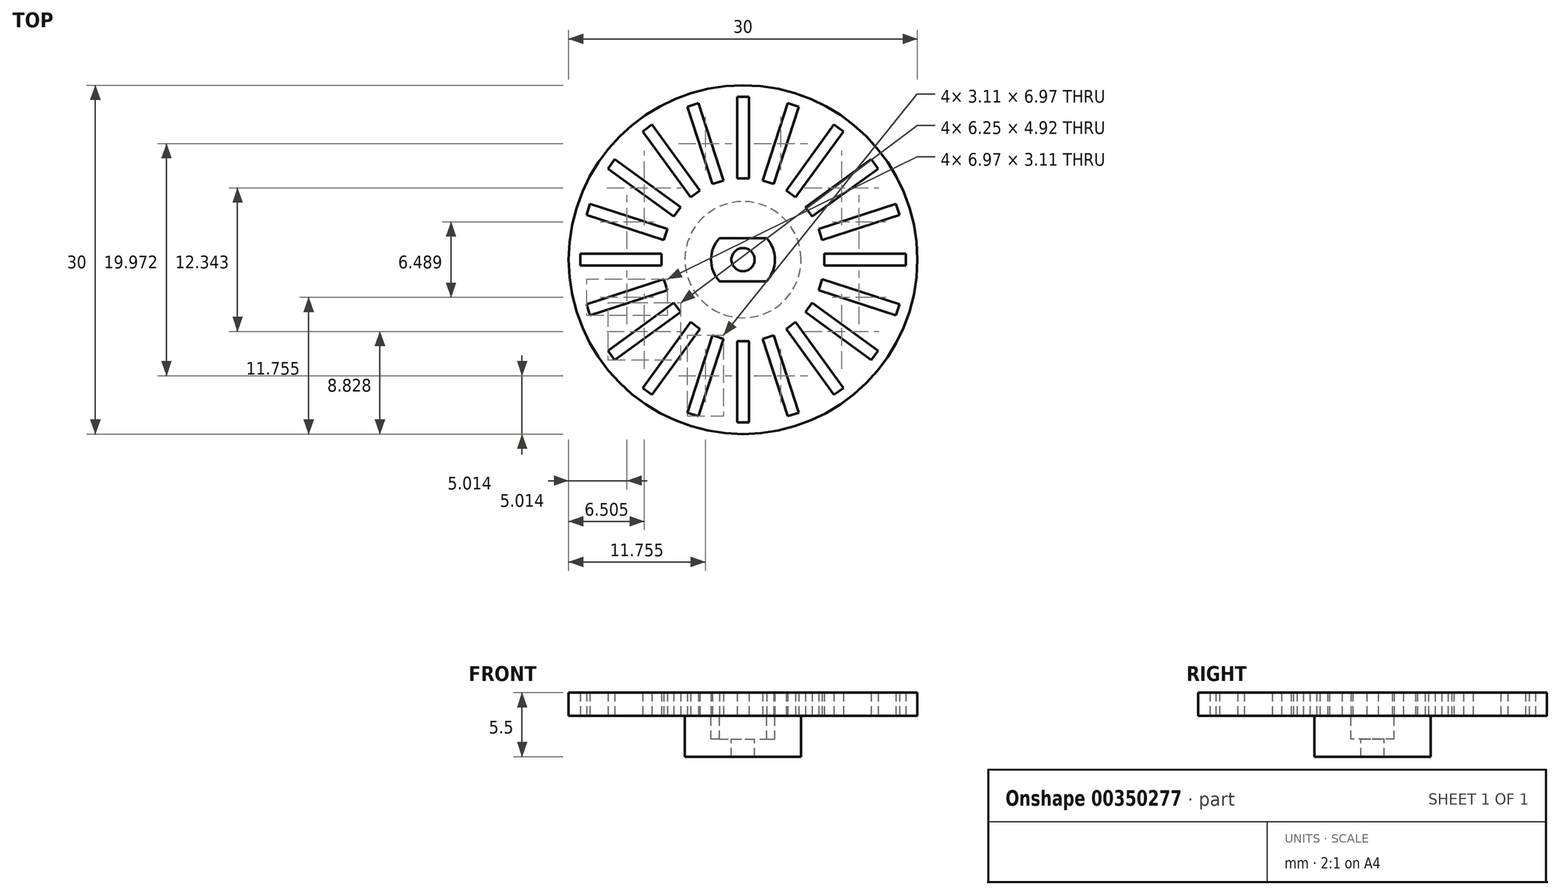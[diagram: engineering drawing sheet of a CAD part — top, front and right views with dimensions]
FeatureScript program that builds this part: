
annotation { "Feature Type Name" : "Feature", "Feature Type Description" : "" }
export const myFeature = defineFeature(function(context is Context, id is Id, definition is map)
    precondition{}
    {
        {
            var Q0;
            Q0=qCreatedBy(makeId("Top.planeOp"),FACE);
            var sketch = newSketch(context, id + "F0", { "sketchPlane" : qUnion([Q0])});
            skCircle(sketch, "E0", {"center": v(0, 0) * mm, "radius": 15 * mm});
            skArc(sketch, "E1", {"start": v(-2.03, 1.86) * mm, "mid": v(-2.75, 0) * mm, "end": v(-2.03, -1.86) * mm});
            skLineSegment(sketch, "E2.MirrorCS", {"start": v(-2.03, -1.86) * mm, "end": v(2.03, -1.86) * mm});
            skArc(sketch, "E3.trimOffspring", {"start": v(2.03, -1.86) * mm, "mid": v(2.75, 0) * mm, "end": v(2.03, 1.86) * mm});
            skLineSegment(sketch, "E4.MirrorCS", {"start": v(-2.03, 1.86) * mm, "end": v(2.03, 1.86) * mm});
            skLineSegment(sketch, "E5", {"start": v(0, -7) * mm, "end": v(-0.5, -7) * mm});
            skLineSegment(sketch, "E6", {"start": v(-0.5, -7) * mm, "end": v(-0.5, -14) * mm});
            skLineSegment(sketch, "E7", {"start": v(-0.5, -14) * mm, "end": v(0, -14) * mm});
            skLineSegment(sketch, "E8.MirrorCS", {"start": v(0.5, -7) * mm, "end": v(0.5, -14) * mm});
            skLineSegment(sketch, "E9", {"start": v(0, -7) * mm, "end": v(0.5, -7) * mm});
            skLineSegment(sketch, "E10", {"start": v(0, -14) * mm, "end": v(0.5, -14) * mm});
            skLineSegment(sketch, "E11.1.0", {"start": v(1.69, -6.81) * mm, "end": v(3.85, -13.47) * mm});
            skLineSegment(sketch, "E11.1.1", {"start": v(2.64, -6.5) * mm, "end": v(4.8, -13.16) * mm});
            skLineSegment(sketch, "E11.1.2", {"start": v(3.85, -13.47) * mm, "end": v(4.33, -13.31) * mm});
            skLineSegment(sketch, "E11.1.3", {"start": v(2.16, -6.66) * mm, "end": v(2.64, -6.5) * mm});
            skLineSegment(sketch, "E11.1.4", {"start": v(4.33, -13.31) * mm, "end": v(4.8, -13.16) * mm});
            skLineSegment(sketch, "E11.1.5", {"start": v(2.16, -6.66) * mm, "end": v(1.69, -6.81) * mm});
            skLineSegment(sketch, "E11.2.0", {"start": v(3.7, -5.96) * mm, "end": v(7.82, -11.62) * mm});
            skLineSegment(sketch, "E11.2.1", {"start": v(4.52, -5.37) * mm, "end": v(8.63, -11.03) * mm});
            skLineSegment(sketch, "E11.2.2", {"start": v(7.82, -11.62) * mm, "end": v(8.23, -11.33) * mm});
            skLineSegment(sketch, "E11.2.3", {"start": v(4.11, -5.66) * mm, "end": v(4.52, -5.37) * mm});
            skLineSegment(sketch, "E11.2.4", {"start": v(8.23, -11.33) * mm, "end": v(8.63, -11.03) * mm});
            skLineSegment(sketch, "E11.2.5", {"start": v(4.11, -5.66) * mm, "end": v(3.7, -5.96) * mm});
            skLineSegment(sketch, "E11.3.0", {"start": v(5.37, -4.52) * mm, "end": v(11.03, -8.63) * mm});
            skLineSegment(sketch, "E11.3.1", {"start": v(5.96, -3.7) * mm, "end": v(11.62, -7.82) * mm});
            skLineSegment(sketch, "E11.3.2", {"start": v(11.03, -8.63) * mm, "end": v(11.33, -8.23) * mm});
            skLineSegment(sketch, "E11.3.3", {"start": v(5.66, -4.11) * mm, "end": v(5.96, -3.7) * mm});
            skLineSegment(sketch, "E11.3.4", {"start": v(11.33, -8.23) * mm, "end": v(11.62, -7.82) * mm});
            skLineSegment(sketch, "E11.3.5", {"start": v(5.66, -4.11) * mm, "end": v(5.37, -4.52) * mm});
            skLineSegment(sketch, "E11.4.0", {"start": v(6.5, -2.64) * mm, "end": v(13.16, -4.8) * mm});
            skLineSegment(sketch, "E11.4.1", {"start": v(6.81, -1.69) * mm, "end": v(13.47, -3.85) * mm});
            skLineSegment(sketch, "E11.4.2", {"start": v(13.16, -4.8) * mm, "end": v(13.31, -4.33) * mm});
            skLineSegment(sketch, "E11.4.3", {"start": v(6.66, -2.16) * mm, "end": v(6.81, -1.69) * mm});
            skLineSegment(sketch, "E11.4.4", {"start": v(13.31, -4.33) * mm, "end": v(13.47, -3.85) * mm});
            skLineSegment(sketch, "E11.4.5", {"start": v(6.66, -2.16) * mm, "end": v(6.5, -2.64) * mm});
            skLineSegment(sketch, "E11.5.0", {"start": v(7, -0.5) * mm, "end": v(14, -0.5) * mm});
            skLineSegment(sketch, "E11.5.1", {"start": v(7, 0.5) * mm, "end": v(14, 0.5) * mm});
            skLineSegment(sketch, "E11.5.2", {"start": v(14, -0.5) * mm, "end": v(14, 0) * mm});
            skLineSegment(sketch, "E11.5.3", {"start": v(7, 0) * mm, "end": v(7, 0.5) * mm});
            skLineSegment(sketch, "E11.5.4", {"start": v(14, 0) * mm, "end": v(14, 0.5) * mm});
            skLineSegment(sketch, "E11.5.5", {"start": v(7, 0) * mm, "end": v(7, -0.5) * mm});
            skLineSegment(sketch, "E11.6.0", {"start": v(6.81, 1.69) * mm, "end": v(13.47, 3.85) * mm});
            skLineSegment(sketch, "E11.6.1", {"start": v(6.5, 2.64) * mm, "end": v(13.16, 4.8) * mm});
            skLineSegment(sketch, "E11.6.2", {"start": v(13.47, 3.85) * mm, "end": v(13.31, 4.33) * mm});
            skLineSegment(sketch, "E11.6.3", {"start": v(6.66, 2.16) * mm, "end": v(6.5, 2.64) * mm});
            skLineSegment(sketch, "E11.6.4", {"start": v(13.31, 4.33) * mm, "end": v(13.16, 4.8) * mm});
            skLineSegment(sketch, "E11.6.5", {"start": v(6.66, 2.16) * mm, "end": v(6.81, 1.69) * mm});
            skLineSegment(sketch, "E11.7.0", {"start": v(5.96, 3.7) * mm, "end": v(11.62, 7.82) * mm});
            skLineSegment(sketch, "E11.7.1", {"start": v(5.37, 4.52) * mm, "end": v(11.03, 8.63) * mm});
            skLineSegment(sketch, "E11.7.2", {"start": v(11.62, 7.82) * mm, "end": v(11.33, 8.23) * mm});
            skLineSegment(sketch, "E11.7.3", {"start": v(5.66, 4.11) * mm, "end": v(5.37, 4.52) * mm});
            skLineSegment(sketch, "E11.7.4", {"start": v(11.33, 8.23) * mm, "end": v(11.03, 8.63) * mm});
            skLineSegment(sketch, "E11.7.5", {"start": v(5.66, 4.11) * mm, "end": v(5.96, 3.7) * mm});
            skLineSegment(sketch, "E11.8.0", {"start": v(4.52, 5.37) * mm, "end": v(8.63, 11.03) * mm});
            skLineSegment(sketch, "E11.8.1", {"start": v(3.7, 5.96) * mm, "end": v(7.82, 11.62) * mm});
            skLineSegment(sketch, "E11.8.2", {"start": v(8.63, 11.03) * mm, "end": v(8.23, 11.33) * mm});
            skLineSegment(sketch, "E11.8.3", {"start": v(4.11, 5.66) * mm, "end": v(3.7, 5.96) * mm});
            skLineSegment(sketch, "E11.8.4", {"start": v(8.23, 11.33) * mm, "end": v(7.82, 11.62) * mm});
            skLineSegment(sketch, "E11.8.5", {"start": v(4.11, 5.66) * mm, "end": v(4.52, 5.37) * mm});
            skLineSegment(sketch, "E11.9.0", {"start": v(2.64, 6.5) * mm, "end": v(4.8, 13.16) * mm});
            skLineSegment(sketch, "E11.9.1", {"start": v(1.69, 6.81) * mm, "end": v(3.85, 13.47) * mm});
            skLineSegment(sketch, "E11.9.2", {"start": v(4.8, 13.16) * mm, "end": v(4.33, 13.31) * mm});
            skLineSegment(sketch, "E11.9.3", {"start": v(2.16, 6.66) * mm, "end": v(1.69, 6.81) * mm});
            skLineSegment(sketch, "E11.9.4", {"start": v(4.33, 13.31) * mm, "end": v(3.85, 13.47) * mm});
            skLineSegment(sketch, "E11.9.5", {"start": v(2.16, 6.66) * mm, "end": v(2.64, 6.5) * mm});
            skLineSegment(sketch, "E11.10.0", {"start": v(0.5, 7) * mm, "end": v(0.5, 14) * mm});
            skLineSegment(sketch, "E11.10.1", {"start": v(-0.5, 7) * mm, "end": v(-0.5, 14) * mm});
            skLineSegment(sketch, "E11.10.2", {"start": v(0.5, 14) * mm, "end": v(0, 14) * mm});
            skLineSegment(sketch, "E11.10.3", {"start": v(0, 7) * mm, "end": v(-0.5, 7) * mm});
            skLineSegment(sketch, "E11.10.4", {"start": v(0, 14) * mm, "end": v(-0.5, 14) * mm});
            skLineSegment(sketch, "E11.10.5", {"start": v(0, 7) * mm, "end": v(0.5, 7) * mm});
            skLineSegment(sketch, "E11.11.0", {"start": v(-1.69, 6.81) * mm, "end": v(-3.85, 13.47) * mm});
            skLineSegment(sketch, "E11.11.1", {"start": v(-2.64, 6.5) * mm, "end": v(-4.8, 13.16) * mm});
            skLineSegment(sketch, "E11.11.2", {"start": v(-3.85, 13.47) * mm, "end": v(-4.33, 13.31) * mm});
            skLineSegment(sketch, "E11.11.3", {"start": v(-2.16, 6.66) * mm, "end": v(-2.64, 6.5) * mm});
            skLineSegment(sketch, "E11.11.4", {"start": v(-4.33, 13.31) * mm, "end": v(-4.8, 13.16) * mm});
            skLineSegment(sketch, "E11.11.5", {"start": v(-2.16, 6.66) * mm, "end": v(-1.69, 6.81) * mm});
            skLineSegment(sketch, "E11.12.0", {"start": v(-3.7, 5.96) * mm, "end": v(-7.82, 11.62) * mm});
            skLineSegment(sketch, "E11.12.1", {"start": v(-4.52, 5.37) * mm, "end": v(-8.63, 11.03) * mm});
            skLineSegment(sketch, "E11.12.2", {"start": v(-7.82, 11.62) * mm, "end": v(-8.23, 11.33) * mm});
            skLineSegment(sketch, "E11.12.3", {"start": v(-4.11, 5.66) * mm, "end": v(-4.52, 5.37) * mm});
            skLineSegment(sketch, "E11.12.4", {"start": v(-8.23, 11.33) * mm, "end": v(-8.63, 11.03) * mm});
            skLineSegment(sketch, "E11.12.5", {"start": v(-4.11, 5.66) * mm, "end": v(-3.7, 5.96) * mm});
            skLineSegment(sketch, "E11.13.0", {"start": v(-5.37, 4.52) * mm, "end": v(-11.03, 8.63) * mm});
            skLineSegment(sketch, "E11.13.1", {"start": v(-5.96, 3.7) * mm, "end": v(-11.62, 7.82) * mm});
            skLineSegment(sketch, "E11.13.2", {"start": v(-11.03, 8.63) * mm, "end": v(-11.33, 8.23) * mm});
            skLineSegment(sketch, "E11.13.3", {"start": v(-5.66, 4.11) * mm, "end": v(-5.96, 3.7) * mm});
            skLineSegment(sketch, "E11.13.4", {"start": v(-11.33, 8.23) * mm, "end": v(-11.62, 7.82) * mm});
            skLineSegment(sketch, "E11.13.5", {"start": v(-5.66, 4.11) * mm, "end": v(-5.37, 4.52) * mm});
            skLineSegment(sketch, "E11.14.0", {"start": v(-6.5, 2.64) * mm, "end": v(-13.16, 4.8) * mm});
            skLineSegment(sketch, "E11.14.1", {"start": v(-6.81, 1.69) * mm, "end": v(-13.47, 3.85) * mm});
            skLineSegment(sketch, "E11.14.2", {"start": v(-13.16, 4.8) * mm, "end": v(-13.31, 4.33) * mm});
            skLineSegment(sketch, "E11.14.3", {"start": v(-6.66, 2.16) * mm, "end": v(-6.81, 1.69) * mm});
            skLineSegment(sketch, "E11.14.4", {"start": v(-13.31, 4.33) * mm, "end": v(-13.47, 3.85) * mm});
            skLineSegment(sketch, "E11.14.5", {"start": v(-6.66, 2.16) * mm, "end": v(-6.5, 2.64) * mm});
            skLineSegment(sketch, "E11.15.0", {"start": v(-7, 0.5) * mm, "end": v(-14, 0.5) * mm});
            skLineSegment(sketch, "E11.15.1", {"start": v(-7, -0.5) * mm, "end": v(-14, -0.5) * mm});
            skLineSegment(sketch, "E11.15.2", {"start": v(-14, 0.5) * mm, "end": v(-14, 0) * mm});
            skLineSegment(sketch, "E11.15.3", {"start": v(-7, 0) * mm, "end": v(-7, -0.5) * mm});
            skLineSegment(sketch, "E11.15.4", {"start": v(-14, 0) * mm, "end": v(-14, -0.5) * mm});
            skLineSegment(sketch, "E11.15.5", {"start": v(-7, 0) * mm, "end": v(-7, 0.5) * mm});
            skLineSegment(sketch, "E11.16.0", {"start": v(-6.81, -1.69) * mm, "end": v(-13.47, -3.85) * mm});
            skLineSegment(sketch, "E11.16.1", {"start": v(-6.5, -2.64) * mm, "end": v(-13.16, -4.8) * mm});
            skLineSegment(sketch, "E11.16.2", {"start": v(-13.47, -3.85) * mm, "end": v(-13.31, -4.33) * mm});
            skLineSegment(sketch, "E11.16.3", {"start": v(-6.66, -2.16) * mm, "end": v(-6.5, -2.64) * mm});
            skLineSegment(sketch, "E11.16.4", {"start": v(-13.31, -4.33) * mm, "end": v(-13.16, -4.8) * mm});
            skLineSegment(sketch, "E11.16.5", {"start": v(-6.66, -2.16) * mm, "end": v(-6.81, -1.69) * mm});
            skLineSegment(sketch, "E11.17.0", {"start": v(-5.96, -3.7) * mm, "end": v(-11.62, -7.82) * mm});
            skLineSegment(sketch, "E11.17.1", {"start": v(-5.37, -4.52) * mm, "end": v(-11.03, -8.63) * mm});
            skLineSegment(sketch, "E11.17.2", {"start": v(-11.62, -7.82) * mm, "end": v(-11.33, -8.23) * mm});
            skLineSegment(sketch, "E11.17.3", {"start": v(-5.66, -4.11) * mm, "end": v(-5.37, -4.52) * mm});
            skLineSegment(sketch, "E11.17.4", {"start": v(-11.33, -8.23) * mm, "end": v(-11.03, -8.63) * mm});
            skLineSegment(sketch, "E11.17.5", {"start": v(-5.66, -4.11) * mm, "end": v(-5.96, -3.7) * mm});
            skLineSegment(sketch, "E11.18.0", {"start": v(-4.52, -5.37) * mm, "end": v(-8.63, -11.03) * mm});
            skLineSegment(sketch, "E11.18.1", {"start": v(-3.7, -5.96) * mm, "end": v(-7.82, -11.62) * mm});
            skLineSegment(sketch, "E11.18.2", {"start": v(-8.63, -11.03) * mm, "end": v(-8.23, -11.33) * mm});
            skLineSegment(sketch, "E11.18.3", {"start": v(-4.11, -5.66) * mm, "end": v(-3.7, -5.96) * mm});
            skLineSegment(sketch, "E11.18.4", {"start": v(-8.23, -11.33) * mm, "end": v(-7.82, -11.62) * mm});
            skLineSegment(sketch, "E11.18.5", {"start": v(-4.11, -5.66) * mm, "end": v(-4.52, -5.37) * mm});
            skLineSegment(sketch, "E11.19.0", {"start": v(-2.64, -6.5) * mm, "end": v(-4.8, -13.16) * mm});
            skLineSegment(sketch, "E11.19.1", {"start": v(-1.69, -6.81) * mm, "end": v(-3.85, -13.47) * mm});
            skLineSegment(sketch, "E11.19.2", {"start": v(-4.8, -13.16) * mm, "end": v(-4.33, -13.31) * mm});
            skLineSegment(sketch, "E11.19.3", {"start": v(-2.16, -6.66) * mm, "end": v(-1.69, -6.81) * mm});
            skLineSegment(sketch, "E11.19.4", {"start": v(-4.33, -13.31) * mm, "end": v(-3.85, -13.47) * mm});
            skLineSegment(sketch, "E11.19.5", {"start": v(-2.16, -6.66) * mm, "end": v(-2.64, -6.5) * mm});
            skSolve(sketch);
        }
        {
            var Q0;
            Q0=qSketchRegion(id+"F0",true);
            var Q1;
            Q1=makeQuery(id+"F0.imprint","IMPRINT",FACE,{"disambiguationData":[TD([[makeQuery(id+"F0.imprint","IMPRINT",EDGE,{"derivedFrom":sQuery(id+"F0.wireOp",EDGE,"E0")}),1.0]])]});
            extrude(context, id + "F1", {"entities" : qUnion([Q0, Q1]), "depth" : 2 * mm});
        }
        {
            var Q0;
            Q0=qCreatedBy(makeId("Top.planeOp"),FACE);
            var sketch = newSketch(context, id + "F2", { "sketchPlane" : qUnion([Q0])});
            skCircle(sketch, "E12", {"center": v(0, 0) * mm, "radius": 5 * mm});
            skSolve(sketch);
        }
        {
            var Q0;
            Q0=makeQuery(id+"F2.imprint","IMPRINT",FACE,{"disambiguationData":[TD([[makeQuery(id+"F2.imprint","IMPRINT",EDGE,{"derivedFrom":sQuery(id+"F2.wireOp",EDGE,"E12")}),1.0]])]});
            extrude(context, id + "F3", {"entities" : qUnion([Q0]), "oppositeDirection" : true, "depth" : 2 * mm});
        }
        {
            var Q0;
            Q0=makeQuery(id+"F0.imprint","IMPRINT",FACE,{"disambiguationData":[TD([[makeQuery(id+"F0.imprint","IMPRINT",EDGE,{"derivedFrom":sQuery(id+"F0.wireOp",EDGE,"E1")}),1.0]])]});
            extrude(context, id + "F4", {"entities" : qUnion([Q0]), "operationType" : NewBodyOperationType.REMOVE, "oppositeDirection" : true, "depth" : 2 * mm});
        }
        {
            var Q0;
            Q0=makeQuery(id+"F3.opExtrude","CAP_FACE",FACE,{"disambiguationData":[OSD([sQuery(id+"F2.wireOp",EDGE,"E12")])],"isStart":false});
            var sketch = newSketch(context, id + "F5", { "sketchPlane" : qUnion([Q0])});
            skCircle(sketch, "E13", {"center": v(0, 0) * mm, "radius": 1 * mm});
            skSolve(sketch);
        }
        {
            var Q0;
            Q0=makeQuery(id+"F5.imprint","IMPRINT",FACE,{"disambiguationData":[TD([[makeQuery(id+"F5.imprint","IMPRINT",EDGE,{"derivedFrom":makeQuery(id+"F3.opExtrude","CAP_EDGE",EDGE,{"disambiguationData":[OSD([sQuery(id+"F2.wireOp",EDGE,"E12")])],"isStart":false})}),-1.0]])]});
            var Q1;
            Q1=makeQuery(id+"F5.imprint","IMPRINT",FACE,{"disambiguationData":[TD([[makeQuery(id+"F5.imprint","IMPRINT",EDGE,{"derivedFrom":sQuery(id+"F5.wireOp",EDGE,"E13")}),-1.0]])]});
            extrude(context, id + "F6", {"entities" : qUnion([Q0, Q1]), "operationType" : NewBodyOperationType.ADD, "depth" : 1.5 * mm});
        }
    });
